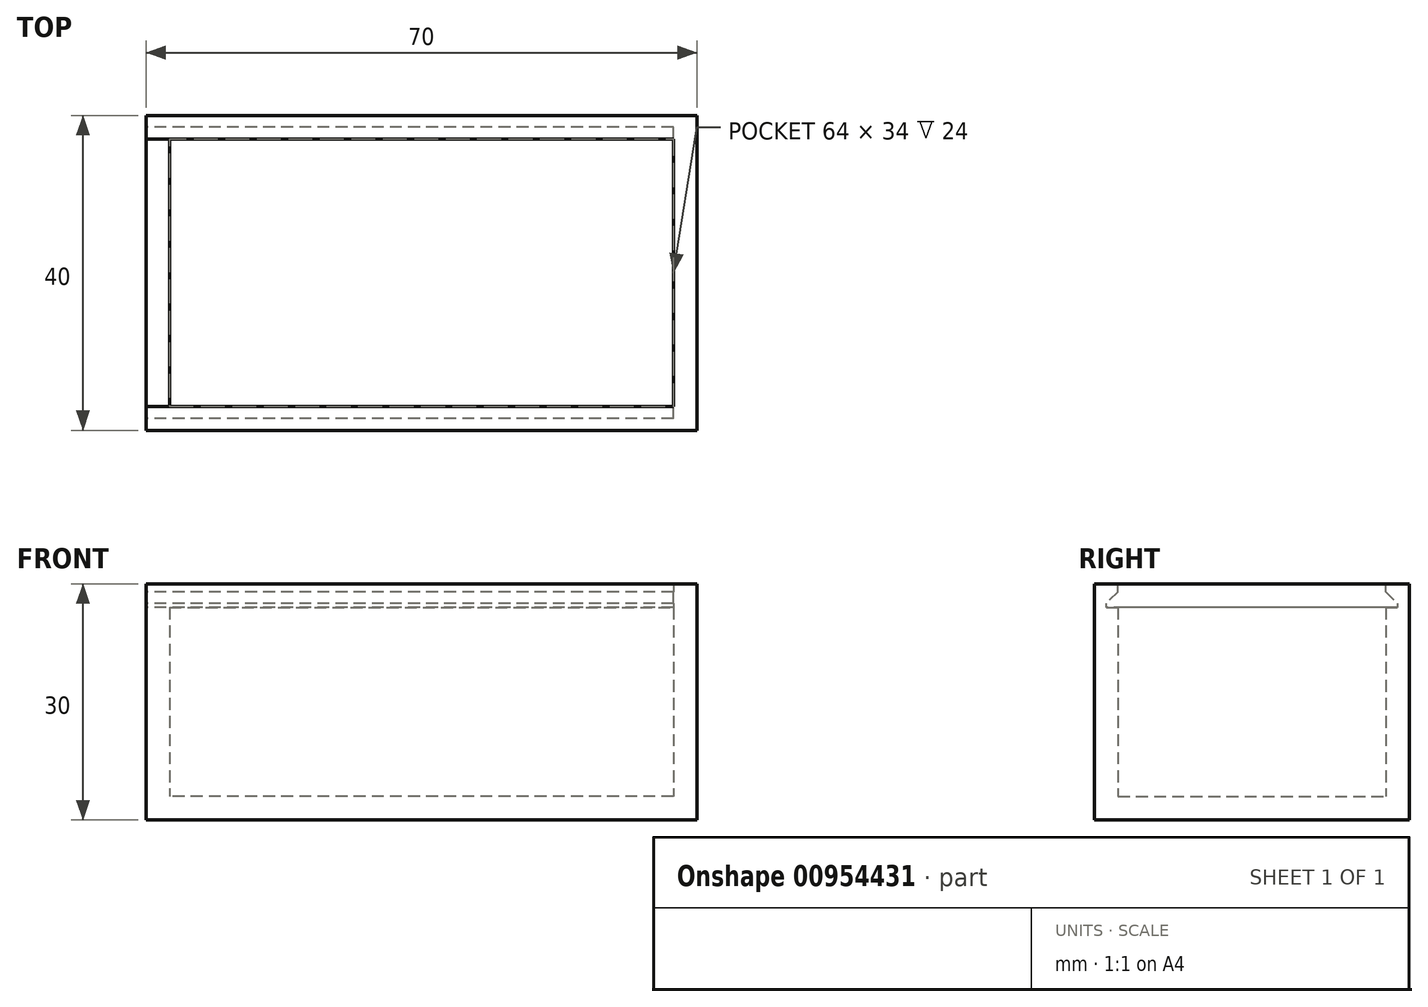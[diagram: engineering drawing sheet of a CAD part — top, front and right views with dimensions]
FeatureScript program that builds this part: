
annotation { "Feature Type Name" : "Feature", "Feature Type Description" : "" }
export const myFeature = defineFeature(function(context is Context, id is Id, definition is map)
    precondition{}
    {
        {
            var Q0;
            Q0=qCreatedBy(makeId("Top.planeOp"),FACE);
            var sketch = newSketch(context, id + "F0", { "sketchPlane" : qUnion([Q0])});
            skLineSegment(sketch, "E0.bottom", {"start": v(35, -20) * mm, "end": v(-35, -20) * mm});
            skLineSegment(sketch, "E0.top", {"start": v(35, 20) * mm, "end": v(-35, 20) * mm});
            skLineSegment(sketch, "E0.left", {"start": v(35, -20) * mm, "end": v(35, 20) * mm});
            skLineSegment(sketch, "E0.right", {"start": v(-35, -20) * mm, "end": v(-35, 20) * mm});
            skPoint(sketch, "E0.middle", {"position": v(0, 0) * mm});
            skSolve(sketch);
        }
        {
            var Q0;
            Q0 = qSketchRegion(id + "F0", true);
            extrude(context, id + "F1", {"entities" : qUnion([Q0]), "depth" : 30 * mm, "offsetDistance" : 25 * mm});
        }
        {
            var Q0;
            Q0=makeQuery(id+"F1.opExtrude","CAP_FACE",FACE,{"disambiguationData":[OSD([sQuery(id+"F0.wireOp",EDGE,"E0.bottom"),sQuery(id+"F0.wireOp",EDGE,"E0.top"),sQuery(id+"F0.wireOp",EDGE,"E0.left"),sQuery(id+"F0.wireOp",EDGE,"E0.right")])],"isStart":false});
            shell(context, id + "F2", {"entities" : qUnion([Q0]), "thickness" : 3 * mm});
        }
        {
            var Q0;
            Q0=makeQuery(id+"F1.opExtrude","SWEPT_FACE",FACE,{"disambiguationData":[OSD([sQuery(id+"F0.wireOp",EDGE,"E0.right")])]});
            var sketch = newSketch(context, id + "F3", { "sketchPlane" : qUnion([Q0])});
            skLineSegment(sketch, "E1", {"start": v(-18.5, 27) * mm, "end": v(18.5, 27) * mm});
            skLineSegment(sketch, "E2", {"start": v(18.5, 27) * mm, "end": v(18.5, 29) * mm});
            skLineSegment(sketch, "E3", {"start": v(18.5, 29) * mm, "end": v(-18.5, 29) * mm});
            skLineSegment(sketch, "E4", {"start": v(-18.5, 29) * mm, "end": v(-18.5, 27) * mm});
            skLineSegment(sketch, "E5", {"start": v(-17, 29) * mm, "end": v(-17, 30) * mm});
            skLineSegment(sketch, "E6", {"start": v(17, 29) * mm, "end": v(17, 30) * mm});
            skLineSegment(sketch, "E7", {"start": v(-17, 30) * mm, "end": v(17, 30) * mm});
            skLineSegment(sketch, "E8", {"start": v(-17, 29) * mm, "end": v(-18.5, 27.5) * mm});
            skLineSegment(sketch, "E9", {"start": v(17, 29) * mm, "end": v(18.5, 27.5) * mm});
            skSolve(sketch);
        }
        {
            var Q0;
            Q0=makeQuery(id+"F3.imprint","IMPRINT",FACE,{"disambiguationData":[TD([[makeQuery(id+"F3.imprint","IMPRINT",EDGE,{"derivedFrom":sQuery(id+"F3.wireOp",EDGE,"E1")}),1.0]])]});
            var Q1;
            {var subQ0=sQuery(id+"F3.wireOp",EDGE,"E5");Q1=makeQuery(id+"F3.imprint","IMPRINT",FACE,{"disambiguationData":[TD([[makeQuery(id+"F3.imprint","IMPRINT",EDGE,{"derivedFrom":subQ0}),-1.0]])]});}
            var Q2;
            Q2=makeQuery(id+"F2.opShell","OFFSET_FACE",FACE,{"disambiguationData":[OSD([sQuery(id+"F0.wireOp",EDGE,"E0.left")])]});
            extrude(context, id + "F4", {"entities" : qUnion([Q0, Q1]), "operationType" : NewBodyOperationType.REMOVE, "endBound" : BoundingType.UP_TO_SURFACE, "oppositeDirection" : true, "depth" : 25 * mm, "endBoundEntityFace" : qUnion([Q2]), "offsetDistance" : 25 * mm});
        }
    });
